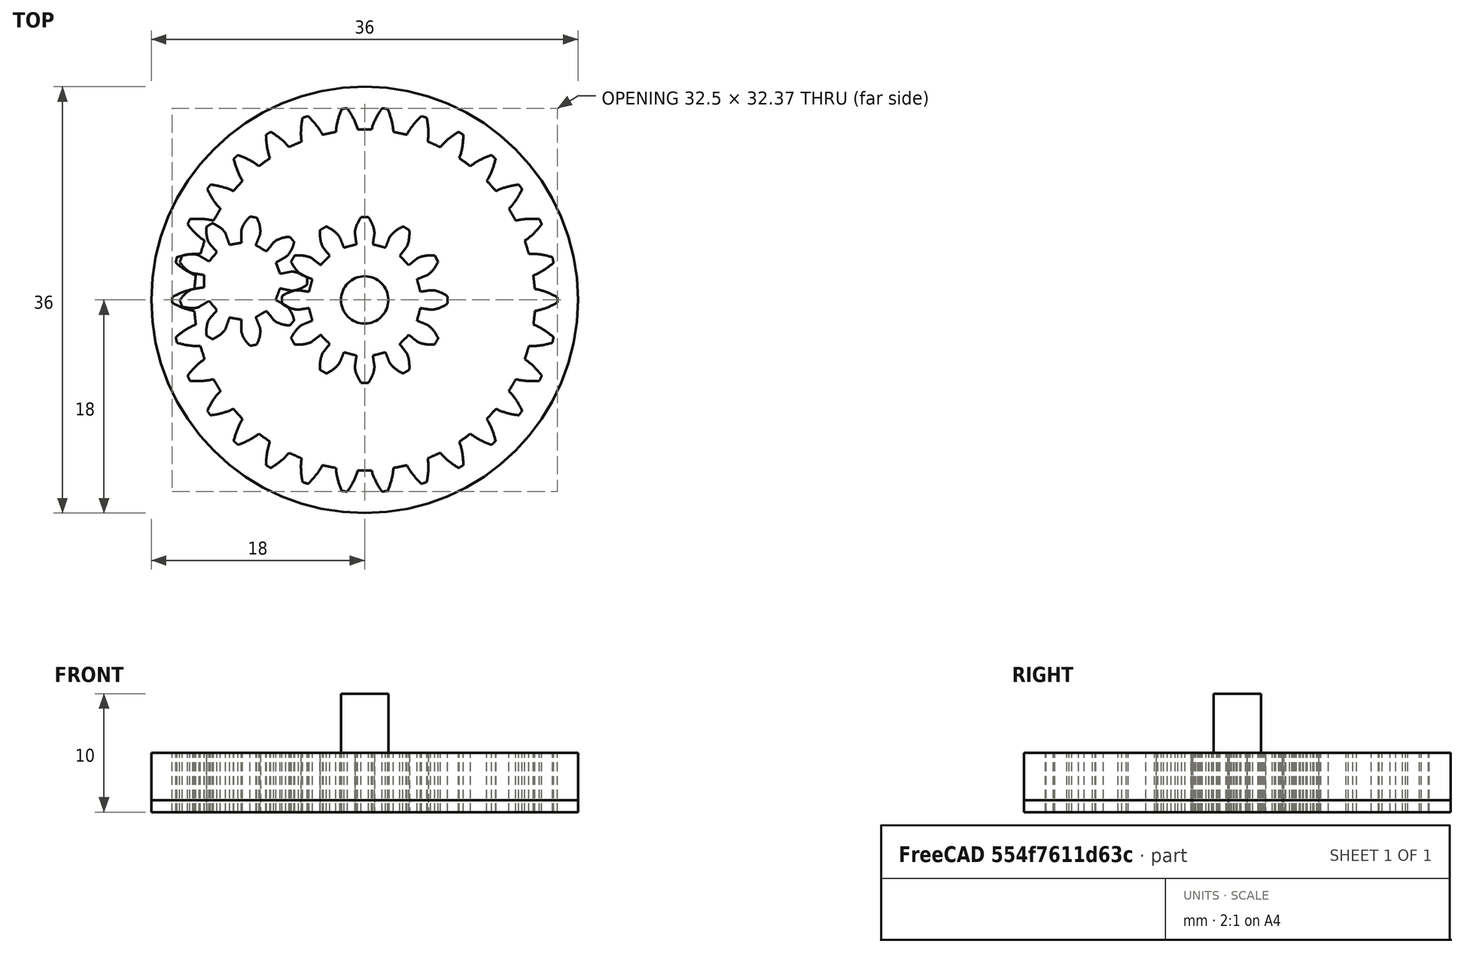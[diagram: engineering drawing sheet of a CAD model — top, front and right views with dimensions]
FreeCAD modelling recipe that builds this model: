
FCSTD DOCUMENT  (FreeCAD 0.19R24276 (Git))
Label: planetary_gear_sholder
License: All rights reserved
LicenseURL: http://en.wikipedia.org/wiki/All_rights_reserved
objects: Part::FeaturePython×3, Part::Cylinder×2
note: 5 computed .brp shape members not serialized (recipe doc carries the construction recipe); baked Part::Feature solids carry a one-line shape summary decoded from their .brp

FEATURE [Part::FeaturePython] InternalInvoluteGear  # WARN: FeaturePython — macro-defined, semantics opaque (R4)
  AttacherType = Attacher::AttachEngine3D
  angular_backlash = 0
  backlash = 0
  beta = 0
  clearance = 0.25
  da = 28.8
  df = 32.5
  double_helix = false
  dw = 30
  head = -0.4
  head_fillet = 0
  height = 5
  module = 1
  numpoints = 6
  outside_diameter = 36
  pressure_angle = 20
  properties_from_tool = false
  reversed_backlash = false
  root_fillet = 0
  shift = 0
  simple = false
  teeth = 30
  thickness = 3
  transverse_pitch = 3.14159
  version = 0.0.4
  expr: angular_backlash = backlash / dw * 360° / pi
FEATURE [Part::FeaturePython] InvoluteGear  # WARN: FeaturePython — macro-defined, semantics opaque (R4)
  AttacherType = Attacher::AttachEngine3D
  Placement = pos=(0,0,0) rot=(0,0,1;0.523599rad)
  angular_backlash = 0
  backlash = 0
  beta = 0
  clearance = 0.25
  da = 14
  df = 9.5
  double_helix = false
  dw = 12
  head = 0
  head_fillet = 0
  height = 5
  module = 1
  numpoints = 6
  pressure_angle = 20
  properties_from_tool = false
  reversed_backlash = false
  root_fillet = 0
  shift = 0
  simple = false
  teeth = 12
  transverse_pitch = 3.14159
  traverse_module = 1
  undercut = false
  version = 0.0.4
  expr: angular_backlash = backlash / dw * 360° / pi
FEATURE [Part::Cylinder] Cylinder  label="subtract c"
  Angle = 360
  AttacherType = Attacher::AttachEngine3D
  Height = 10
  Radius = 2
FEATURE [Part::FeaturePython] InvoluteGear001  # WARN: FeaturePython — macro-defined, semantics opaque (R4)
  AttacherType = Attacher::AttachEngine3D
  Placement = pos=(-10.34,1.58589,0) rot=(0,0,1;0rad)
  angular_backlash = 0
  backlash = 0
  beta = 0
  clearance = 0.25
  da = 11
  df = 6.5
  double_helix = false
  dw = 9
  head = 0
  head_fillet = 0
  height = 5
  module = 1
  numpoints = 6
  pressure_angle = 20
  properties_from_tool = false
  reversed_backlash = false
  root_fillet = 0
  shift = 0
  simple = false
  teeth = 9
  transverse_pitch = 3.14159
  traverse_module = 1
  undercut = false
  version = 0.0.4
  expr: angular_backlash = backlash / dw * 360° / pi
FEATURE [Part::Cylinder] Cylinder001  label="Cylinder"
  Angle = 360
  AttacherType = Attacher::AttachEngine3D
  Height = 1
  Radius = 18
